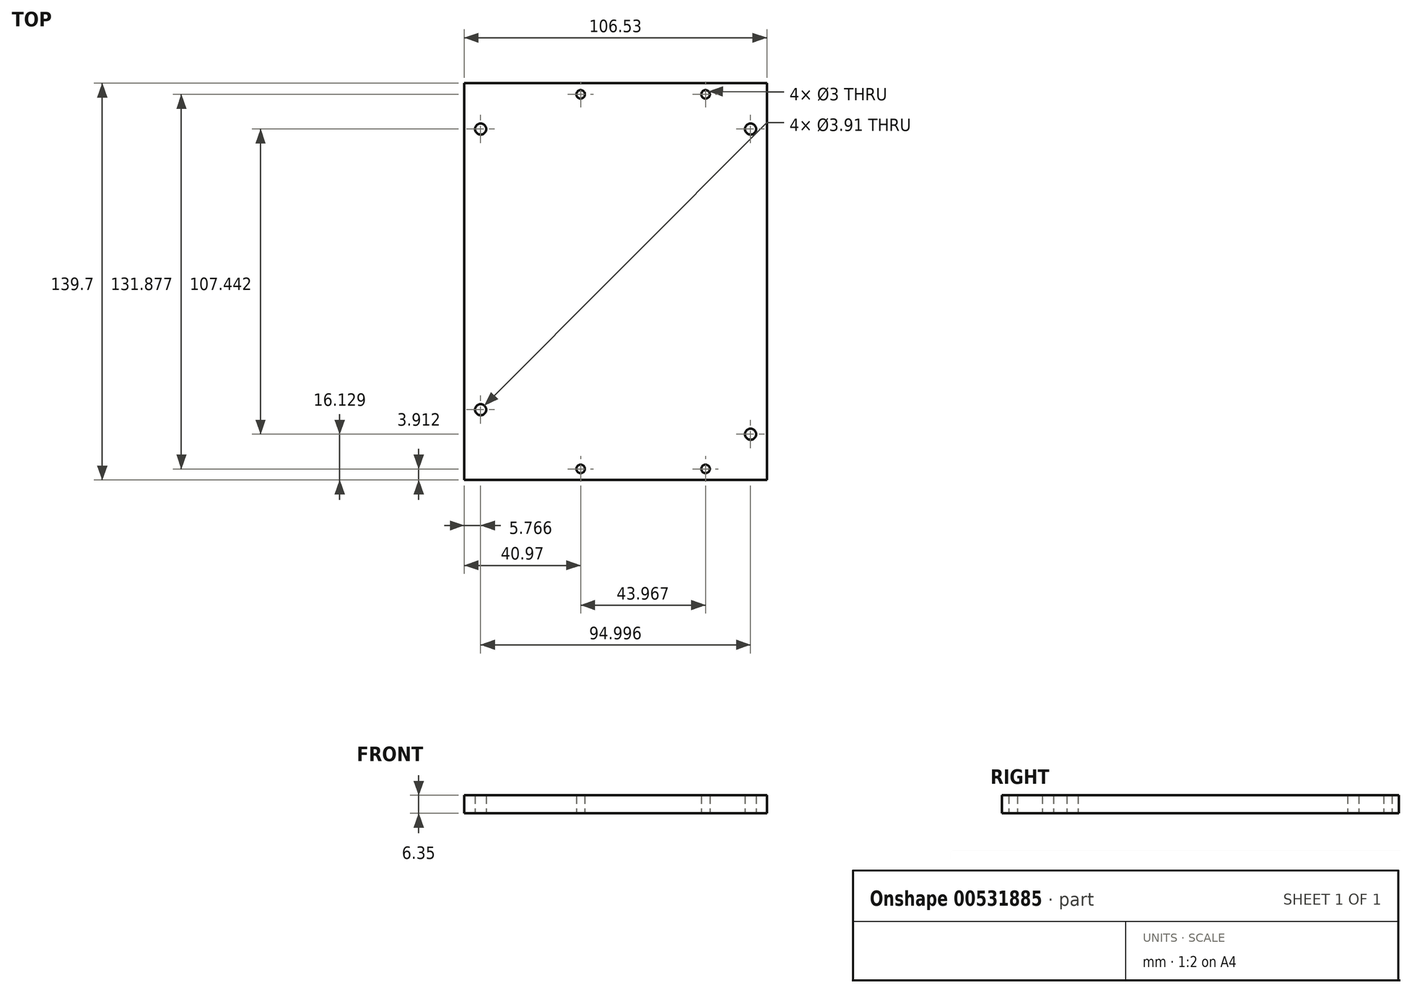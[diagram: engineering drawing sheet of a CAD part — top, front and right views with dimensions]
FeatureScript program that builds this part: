
annotation { "Feature Type Name" : "Feature", "Feature Type Description" : "" }
export const myFeature = defineFeature(function(context is Context, id is Id, definition is map)
    precondition{}
    {
        {
            var Q0;
            Q0=qCreatedBy(makeId("Top.planeOp"),FACE);
            var sketch = newSketch(context, id + "F0", { "sketchPlane" : qUnion([Q0])});
            skLineSegment(sketch, "E0.bottom", {"start": v(0, 0) * mm, "end": v(106.53, 0) * mm});
            skLineSegment(sketch, "E0.top", {"start": v(0, -139.7) * mm, "end": v(106.53, -139.7) * mm});
            skLineSegment(sketch, "E0.left", {"start": v(0, 0) * mm, "end": v(0, -139.7) * mm});
            skLineSegment(sketch, "E0.right", {"start": v(106.53, 0) * mm, "end": v(106.53, -139.7) * mm});
            skCircle(sketch, "E1", {"center": v(40.97, -3.91) * mm, "radius": 1.5 * mm});
            skLineSegment(sketch, "E2", {"start": v(40.97, -3.91) * mm, "end": v(84.94, -3.91) * mm, "construction": true});
            skCircle(sketch, "E3", {"center": v(84.94, -3.91) * mm, "radius": 1.5 * mm});
            skLineSegment(sketch, "E4", {"start": v(40.97, -3.91) * mm, "end": v(40.97, -135.79) * mm, "construction": true});
            skCircle(sketch, "E5", {"center": v(40.97, -135.79) * mm, "radius": 1.5 * mm});
            skLineSegment(sketch, "E6", {"start": v(84.94, -3.91) * mm, "end": v(84.94, -135.79) * mm, "construction": true});
            skCircle(sketch, "E7", {"center": v(84.94, -135.79) * mm, "radius": 1.5 * mm});
            skLineSegment(sketch, "E8", {"start": v(40.97, -135.79) * mm, "end": v(84.94, -135.79) * mm, "construction": true});
            skLineSegment(sketch, "E9", {"start": v(0, -69.85) * mm, "end": v(40.97, -69.85) * mm, "construction": true});
            skCircle(sketch, "E10", {"center": v(5.77, -16.13) * mm, "radius": 1.96 * mm});
            skCircle(sketch, "E11", {"center": v(100.76, -16.13) * mm, "radius": 1.96 * mm});
            skLineSegment(sketch, "E12", {"start": v(5.77, -16.13) * mm, "end": v(100.76, -16.13) * mm, "construction": true});
            skLineSegment(sketch, "E13", {"start": v(100.76, -16.13) * mm, "end": v(100.76, -123.57) * mm, "construction": true});
            skCircle(sketch, "E14", {"center": v(100.76, -123.57) * mm, "radius": 1.96 * mm});
            skLineSegment(sketch, "E15", {"start": v(5.77, -16.13) * mm, "end": v(5.77, -114.94) * mm, "construction": true});
            skCircle(sketch, "E16", {"center": v(5.77, -114.94) * mm, "radius": 1.96 * mm});
            skLineSegment(sketch, "E17", {"start": v(100.76, -69.85) * mm, "end": v(106.53, -69.85) * mm, "construction": true});
            skSolve(sketch);
        }
        {
            var Q0;
            Q0=makeQuery(id+"F0.imprint","IMPRINT",FACE,{"disambiguationData":[TD([[makeQuery(id+"F0.imprint","IMPRINT",EDGE,{"derivedFrom":sQuery(id+"F0.wireOp",EDGE,"E0.bottom")}),-1.0]])]});
            extrude(context, id + "F1", {"entities" : qUnion([Q0]), "depth" : 6.35 * mm, "offsetDistance" : 25.4 * mm});
        }
    });
